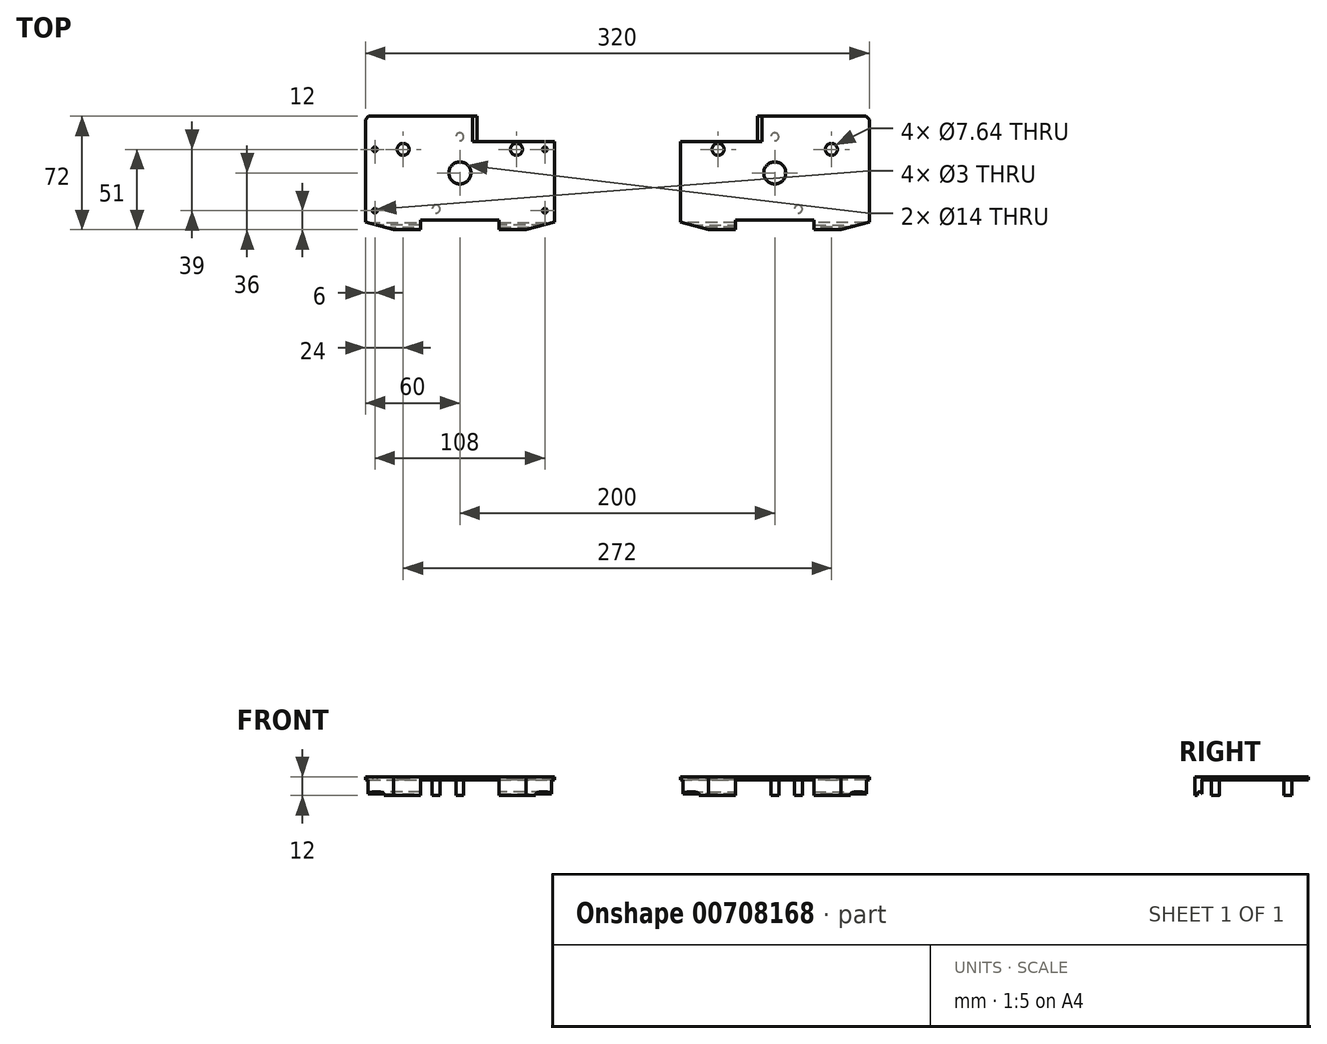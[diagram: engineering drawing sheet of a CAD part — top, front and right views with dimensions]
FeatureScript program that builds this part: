
annotation { "Feature Type Name" : "Feature", "Feature Type Description" : "" }
export const myFeature = defineFeature(function(context is Context, id is Id, definition is map)
    precondition{}
    {
        {
            var Q0;
            Q0=qCreatedBy(makeId("Top.planeOp"),FACE);
            var sketch = newSketch(context, id + "F0", { "sketchPlane" : qUnion([Q0])});
            skLineSegment(sketch, "E0.bottom", {"start": v(-60, 36) * mm, "end": v(60, 36) * mm});
            skLineSegment(sketch, "E0.top", {"start": v(-60, -36) * mm, "end": v(60, -36) * mm});
            skLineSegment(sketch, "E0.left", {"start": v(-60, 36) * mm, "end": v(-60, -36) * mm, "construction": true});
            skLineSegment(sketch, "E0.right", {"start": v(60, 36) * mm, "end": v(60, -36) * mm, "construction": true});
            skCircle(sketch, "E1", {"center": v(0, 0) * mm, "radius": 7 * mm});
            skLineSegment(sketch, "E2", {"start": v(-60, 0) * mm, "end": v(60, 0) * mm, "construction": true});
            skCircle(sketch, "E3", {"center": v(0, 23) * mm, "radius": 2.4 * mm, "construction": true});
            skCircle(sketch, "E4.0.MirrorC", {"center": v(0, -23) * mm, "radius": 2.4 * mm, "construction": true});
            skCircle(sketch, "E5.0.MirrorC", {"center": v(-15, 23) * mm, "radius": 2.5 * mm, "construction": true});
            skCircle(sketch, "E6.0.MirrorC", {"center": v(-15, -23) * mm, "radius": 2.5 * mm, "construction": true});
            skLineSegment(sketch, "E7.bottom", {"start": v(-22.32, 36) * mm, "end": v(10.24, 36) * mm, "construction": true});
            skLineSegment(sketch, "E7.top", {"start": v(-23.32, -36) * mm, "end": v(9.24, -36) * mm, "construction": true});
            skLineSegment(sketch, "E8.left", {"start": v(-60, 36) * mm, "end": v(-60, -36) * mm});
            skLineSegment(sketch, "E8.right", {"start": v(60, 36) * mm, "end": v(60, -36) * mm});
            skLineSegment(sketch, "E9.bottom", {"start": v(-60, 36) * mm, "end": v(-42, 36) * mm, "construction": true});
            skLineSegment(sketch, "E9.top", {"start": v(-60, -36) * mm, "end": v(-42, -36) * mm, "construction": true});
            skLineSegment(sketch, "E9.right", {"start": v(-42, 36) * mm, "end": v(-42, -36) * mm, "construction": true});
            skCircle(sketch, "E10", {"center": v(-36, 15) * mm, "radius": 3.82 * mm});
            skCircle(sketch, "E11.0.MirrorC", {"center": v(36, 15) * mm, "radius": 3.82 * mm});
            skLineSegment(sketch, "E12.bottom", {"start": v(10, -36) * mm, "end": v(-10, -36) * mm});
            skLineSegment(sketch, "E13", {"start": v(0, 23) * mm, "end": v(0, -23) * mm, "construction": true});
            skLineSegment(sketch, "E14", {"start": v(-36, 15) * mm, "end": v(0, 15) * mm, "construction": true});
            skLineSegment(sketch, "E15", {"start": v(0, 15) * mm, "end": v(36, 15) * mm, "construction": true});
            skCircle(sketch, "E16", {"center": v(-54, -24) * mm, "radius": 1.5 * mm, "construction": true});
            skCircle(sketch, "E17", {"center": v(-54, 15) * mm, "radius": 1.5 * mm, "construction": true});
            skLineSegment(sketch, "E18", {"start": v(-36, 15) * mm, "end": v(-56.54, 15) * mm, "construction": true});
            skLineSegment(sketch, "E19", {"start": v(-54, -24) * mm, "end": v(-54, 15) * mm, "construction": true});
            skCircle(sketch, "E20.0.MirrorC", {"center": v(54, 15) * mm, "radius": 1.5 * mm, "construction": true});
            skCircle(sketch, "E21.0.MirrorC", {"center": v(54, -24) * mm, "radius": 1.5 * mm, "construction": true});
            skSolve(sketch);
        }
        {
            var Q0;
            Q0=makeQuery(id+"F0.imprint","IMPRINT",FACE,{"disambiguationData":[TD([[makeQuery(id+"F0.imprint","IMPRINT",EDGE,{"derivedFrom":sQuery(id+"F0.wireOp",EDGE,"E1")}),-1.0]])]});
            extrude(context, id + "F1", {"entities" : qUnion([Q0]), "depth" : 12 * mm});
        }
        {
            var Q0;
            Q0=makeQuery(id+"F1.opExtrude","CAP_FACE",FACE,{"disambiguationData":[OSD([sQuery(id+"F0.wireOp",EDGE,"E1"),sQuery(id+"F0.wireOp",EDGE,"E0.bottom"),sQuery(id+"F0.wireOp",EDGE,"E0.top"),sQuery(id+"F0.wireOp",EDGE,"E8.left"),sQuery(id+"F0.wireOp",EDGE,"E8.right"),sQuery(id+"F0.wireOp",EDGE,"E10"),sQuery(id+"F0.wireOp",EDGE,"E11.0.MirrorC"),sQuery(id+"F0.wireOp",EDGE,"E12.bottom")])],"isStart":false});
            var sketch = newSketch(context, id + "F2", { "sketchPlane" : qUnion([Q0])});
            skLineSegment(sketch, "E22", {"start": v(60, 20) * mm, "end": v(60, 36) * mm});
            skLineSegment(sketch, "E23", {"start": v(60, 36) * mm, "end": v(-42, 36) * mm});
            skLineSegment(sketch, "E24", {"start": v(-60, -36) * mm, "end": v(60, -36) * mm});
            skLineSegment(sketch, "E25", {"start": v(-42, 20) * mm, "end": v(60, 20) * mm});
            skLineSegment(sketch, "E26", {"start": v(60, -36) * mm, "end": v(-60, -36) * mm});
            skLineSegment(sketch, "E27", {"start": v(-60, 36) * mm, "end": v(-42, 36) * mm, "construction": true});
            skLineSegment(sketch, "E28", {"start": v(60, 36) * mm, "end": v(60, 20) * mm});
            skLineSegment(sketch, "E29", {"start": v(-42, 36) * mm, "end": v(-42, 27) * mm, "construction": true});
            skLineSegment(sketch, "E30", {"start": v(-42, 27) * mm, "end": v(-46, 27) * mm, "construction": true});
            skLineSegment(sketch, "E31", {"start": v(-46, 27) * mm, "end": v(-46, 20) * mm, "construction": true});
            skLineSegment(sketch, "E32", {"start": v(-46, 20) * mm, "end": v(-42, 20) * mm, "construction": true});
            skSolve(sketch);
        }
        {
            var Q0;
            Q0=makeQuery(id+"F0.imprint","IMPRINT",FACE,{"disambiguationData":[TD([[makeQuery(id+"F0.imprint","IMPRINT",EDGE,{"derivedFrom":sQuery(id+"F0.wireOp",EDGE,"E1")}),-1.0]])]});
            var sketch = newSketch(context, id + "F3", { "sketchPlane" : qUnion([Q0])});
            skLineSegment(sketch, "E33.bottom", {"start": v(25, -36) * mm, "end": v(-25, -36) * mm});
            skLineSegment(sketch, "E33.top", {"start": v(25, -30) * mm, "end": v(-25, -30) * mm});
            skLineSegment(sketch, "E33.left", {"start": v(25, -36) * mm, "end": v(25, -30) * mm});
            skLineSegment(sketch, "E33.right", {"start": v(-25, -36) * mm, "end": v(-25, -30) * mm});
            skLineSegment(sketch, "E34", {"start": v(-25, -33) * mm, "end": v(0, -33) * mm, "construction": true});
            skLineSegment(sketch, "E35", {"start": v(0, -33) * mm, "end": v(25, -33) * mm, "construction": true});
            skLineSegment(sketch, "E36", {"start": v(0, -22.48) * mm, "end": v(0, -36) * mm, "construction": true});
            skSolve(sketch);
        }
        {
            var Q0;
            Q0=makeQuery(id+"F3.imprint","IMPRINT",FACE,{"disambiguationData":[TD([[makeQuery(id+"F3.imprint","IMPRINT",EDGE,{"derivedFrom":sQuery(id+"F3.wireOp",EDGE,"E33.top")}),1.0]])]});
            var Q1;
            Q1=makeQuery(id+"F1.opExtrude","CAP_FACE",FACE,{"disambiguationData":[OSD([sQuery(id+"F0.wireOp",EDGE,"E1"),sQuery(id+"F0.wireOp",EDGE,"E0.bottom"),sQuery(id+"F0.wireOp",EDGE,"E0.top"),sQuery(id+"F0.wireOp",EDGE,"E8.left"),sQuery(id+"F0.wireOp",EDGE,"E8.right"),sQuery(id+"F0.wireOp",EDGE,"E10"),sQuery(id+"F0.wireOp",EDGE,"E11.0.MirrorC"),sQuery(id+"F0.wireOp",EDGE,"E12.bottom")])],"isStart":false});
            extrude(context, id + "F4", {"entities" : qUnion([Q0]), "operationType" : NewBodyOperationType.REMOVE, "endBound" : BoundingType.UP_TO_SURFACE, "endBoundEntityFace" : qUnion([Q1]), "depth" : 25 * mm});
        }
        {
            var Q0;
            Q0=makeQuery(id+"F0.imprint","IMPRINT",FACE,{"disambiguationData":[TD([[makeQuery(id+"F0.imprint","IMPRINT",EDGE,{"derivedFrom":sQuery(id+"F0.wireOp",EDGE,"E1")}),-1.0]])]});
            var sketch = newSketch(context, id + "F5", { "sketchPlane" : qUnion([Q0])});
            skLineSegment(sketch, "E37.bottom", {"start": v(-60, -31.62) * mm, "end": v(60, -31.63) * mm});
            skLineSegment(sketch, "E37.top", {"start": v(-60, -34.37) * mm, "end": v(60, -34.38) * mm});
            skLineSegment(sketch, "E37.left", {"start": v(-60, -31.62) * mm, "end": v(-60, -34.37) * mm});
            skLineSegment(sketch, "E37.right", {"start": v(60, -31.63) * mm, "end": v(60, -34.38) * mm});
            skLineSegment(sketch, "E38", {"start": v(8.47, -31.63) * mm, "end": v(8.47, -30) * mm, "construction": true});
            skLineSegment(sketch, "E39", {"start": v(8.43, -34.38) * mm, "end": v(8.43, -36) * mm, "construction": true});
            skSolve(sketch);
        }
        {
            var Q0;
            Q0=makeQuery(id+"F5.imprint","IMPRINT",FACE,{"disambiguationData":[TD([[makeQuery(id+"F5.imprint","IMPRINT",EDGE,{"derivedFrom":sQuery(id+"F5.wireOp",EDGE,"E37.bottom")}),-1.0]])]});
            extrude(context, id + "F6", {"entities" : qUnion([Q0]), "operationType" : NewBodyOperationType.REMOVE, "depth" : 2.5 * mm});
        }
        {
            var Q0;
            Q0=makeQuery(id+"F6.boolean.opBoolean","COPY",EDGE,{"disambiguationData":[OD(1.0)],"derivedFrom":makeQuery(id+"F6.opExtrude","CAP_EDGE",EDGE,{"disambiguationData":[OSD([sQuery(id+"F5.wireOp",EDGE,"E37.bottom")])],"isStart":false})});
            var Q1;
            Q1=makeQuery(id+"F6.boolean.opBoolean","COPY",EDGE,{"disambiguationData":[OD(1.0)],"derivedFrom":makeQuery(id+"F6.opExtrude","CAP_EDGE",EDGE,{"disambiguationData":[OSD([sQuery(id+"F5.wireOp",EDGE,"E37.top")])],"isStart":false})});
            var Q2;
            Q2=makeQuery(id+"F6.boolean.opBoolean","COPY",EDGE,{"disambiguationData":[OD(0.0)],"derivedFrom":makeQuery(id+"F6.opExtrude","CAP_EDGE",EDGE,{"disambiguationData":[OSD([sQuery(id+"F5.wireOp",EDGE,"E37.top")])],"isStart":false})});
            var Q3;
            Q3=makeQuery(id+"F6.boolean.opBoolean","COPY",EDGE,{"disambiguationData":[OD(0.0)],"derivedFrom":makeQuery(id+"F6.opExtrude","CAP_EDGE",EDGE,{"disambiguationData":[OSD([sQuery(id+"F5.wireOp",EDGE,"E37.bottom")])],"isStart":false})});
            fillet(context, id + "F7", {"entities" : qUnion([Q0, Q1, Q2, Q3]), "radius" : 1.5 * mm, "tangentPropagation" : true, "allowEdgeOverflow" : false});
        }
        {
            var Q0;
            Q0=makeQuery(id+"F1.opExtrude","SWEPT_FACE",FACE,{"disambiguationData":[OSD([sQuery(id+"F0.wireOp",EDGE,"E0.bottom")])]});
            var sketch = newSketch(context, id + "F8", { "sketchPlane" : qUnion([Q0])});
            skLineSegment(sketch, "E40", {"start": v(-60, 6) * mm, "end": v(-38.5, 6) * mm, "construction": true});
            skLineSegment(sketch, "E41", {"start": v(0, 0) * mm, "end": v(0, 12) * mm, "construction": true});
            skLineSegment(sketch, "E42", {"start": v(-8, 0) * mm, "end": v(-8, 12) * mm, "construction": true});
            skLineSegment(sketch, "E43", {"start": v(-8, 12) * mm, "end": v(-60, 12) * mm});
            skLineSegment(sketch, "E44", {"start": v(-60, 2) * mm, "end": v(-60, 12) * mm});
            skLineSegment(sketch, "E45", {"start": v(-8, 2) * mm, "end": v(-23.25, 2) * mm, "construction": true});
            skLineSegment(sketch, "E46", {"start": v(-23.25, 2) * mm, "end": v(-38.5, 2) * mm, "construction": true});
            skLineSegment(sketch, "E47", {"start": v(-38.5, 6) * mm, "end": v(-38.5, 0) * mm, "construction": true});
            skLineSegment(sketch, "E48", {"start": v(-60, 2) * mm, "end": v(-23.25, 2) * mm});
            skLineSegment(sketch, "E49", {"start": v(-23.25, 2) * mm, "end": v(-8, 12) * mm});
            skSolve(sketch);
        }
        {
            var Q0;
            Q0=makeQuery(id+"F8.imprint","IMPRINT",FACE,{"disambiguationData":[TD([[makeQuery(id+"F8.imprint","IMPRINT",EDGE,{"derivedFrom":sQuery(id+"F8.wireOp",EDGE,"E43")}),1.0]])]});
            extrude(context, id + "F9", {"entities" : qUnion([Q0]), "operationType" : NewBodyOperationType.REMOVE, "oppositeDirection" : true, "depth" : 16 * mm});
        }
        {
            var Q0;
            Q0=makeQuery(id+"F9.boolean.opBoolean","COPY",EDGE,{"derivedFrom":makeQuery(id+"F9.opExtrude","SWEPT_EDGE",EDGE,{"disambiguationData":[OSD([sQuery(id+"F8.wireOp",EDGE,"dc820323-19ea-4039-b468-714fe8b4bf2b"),sQuery(id+"F8.wireOp",EDGE,"f9c62189-2ec5-4655-88e0-a14efa9e9823")])]})});
            var Q1;
            Q1=makeQuery(id+"F9.boolean.opBoolean","COPY",EDGE,{"derivedFrom":makeQuery(id+"F9.opExtrude","SWEPT_EDGE",EDGE,{"disambiguationData":[OSD([sQuery(id+"F2.wireOp",EDGE,"E23"),sQuery(id+"F8.wireOp",EDGE,"f9c62189-2ec5-4655-88e0-a14efa9e9823"),sQuery(id+"F8.wireOp",EDGE,"E43")])]})});
            var Q2;
            Q2=makeQuery(id+"F9.boolean.opBoolean","COPY",EDGE,{"derivedFrom":makeQuery(id+"F9.opExtrude","SWEPT_EDGE",EDGE,{"disambiguationData":[OSD([sQuery(id+"F8.wireOp",EDGE,"E48"),sQuery(id+"F8.wireOp",EDGE,"E49")])]})});
            var Q3;
            Q3=makeQuery(id+"F9.boolean.opBoolean","COPY",EDGE,{"derivedFrom":makeQuery(id+"F9.opExtrude","SWEPT_EDGE",EDGE,{"disambiguationData":[OSD([sQuery(id+"F0.wireOp",EDGE,"E0.bottom"),sQuery(id+"F8.wireOp",EDGE,"E43"),sQuery(id+"F8.wireOp",EDGE,"E49")])]})});
            fillet(context, id + "F10", {"entities" : qUnion([Q0, Q1, Q2, Q3]), "radius" : 5 * mm, "tangentPropagation" : true, "allowEdgeOverflow" : false});
        }
        {
            var Q0;
            {var subQ0=sQuery(id+"F0.wireOp",EDGE,"E1");var subQ1=sQuery(id+"F0.wireOp",EDGE,"E0.bottom");var subQ2=sQuery(id+"F0.wireOp",EDGE,"E8.left");var subQ3=sQuery(id+"F0.wireOp",EDGE,"E8.right");var subQ4=sQuery(id+"F0.wireOp",EDGE,"E10");var subQ5=sQuery(id+"F0.wireOp",EDGE,"E11.0.MirrorC");Q0=makeQuery(id+"F6.boolean.opBoolean","SPLIT",FACE,{"disambiguationData":[TD([makeQuery(id+"F1.opExtrude","SWEPT_FACE",FACE,{"disambiguationData":[OSD([subQ0])]}),makeQuery(id+"F1.opExtrude","SWEPT_FACE",FACE,{"disambiguationData":[OSD([subQ1])]}),makeQuery(id+"F1.opExtrude","SWEPT_FACE",FACE,{"disambiguationData":[OSD([subQ2])]}),makeQuery(id+"F1.opExtrude","SWEPT_FACE",FACE,{"disambiguationData":[OSD([subQ3])]}),makeQuery(id+"F1.opExtrude","SWEPT_FACE",FACE,{"disambiguationData":[OSD([subQ4])]}),makeQuery(id+"F1.opExtrude","SWEPT_FACE",FACE,{"disambiguationData":[OSD([subQ5])]}),makeQuery(id+"F4.boolean.opBoolean","COPY",FACE,{"derivedFrom":makeQuery(id+"F4.opExtrude","SWEPT_FACE",FACE,{"disambiguationData":[OSD([sQuery(id+"F3.wireOp",EDGE,"E33.top")])]})}),makeQuery(id+"F4.boolean.opBoolean","COPY",FACE,{"derivedFrom":makeQuery(id+"F4.opExtrude","SWEPT_FACE",FACE,{"disambiguationData":[OSD([sQuery(id+"F3.wireOp",EDGE,"E33.left")])]})}),makeQuery(id+"F4.boolean.opBoolean","COPY",FACE,{"derivedFrom":makeQuery(id+"F4.opExtrude","SWEPT_FACE",FACE,{"disambiguationData":[OSD([sQuery(id+"F3.wireOp",EDGE,"E33.right")])]})}),makeQuery(id+"F6.opExtrude","SWEPT_FACE",FACE,{"disambiguationData":[OSD([sQuery(id+"F5.wireOp",EDGE,"E37.bottom")])]})])],"derivedFrom":makeQuery(id+"F1.opExtrude","CAP_FACE",FACE,{"disambiguationData":[OSD([subQ0,subQ1,sQuery(id+"F0.wireOp",EDGE,"E0.top"),subQ2,subQ3,subQ4,subQ5,sQuery(id+"F0.wireOp",EDGE,"E12.bottom")])],"isStart":true})});}
            var sketch = newSketch(context, id + "F11", { "sketchPlane" : qUnion([Q0])});
            skCircle(sketch, "E50", {"center": v(-15.05, -22.91) * mm, "radius": 2.5 * mm});
            skCircle(sketch, "E51.0.MirrorC", {"center": v(-0.05, -23) * mm, "radius": 2.5 * mm});
            skCircle(sketch, "E52.0.MirrorC", {"center": v(-15.05, 22.91) * mm, "radius": 2.5 * mm});
            skCircle(sketch, "E53.0.MirrorC", {"center": v(-0.05, 23) * mm, "radius": 2.5 * mm});
            skSolve(sketch);
        }
        {
            var Q0;
            {Q0=qUnion([makeQuery(id+"F11.imprint","IMPRINT",FACE,{"disambiguationData":[TD([[makeQuery(id+"F11.imprint","IMPRINT",EDGE,{"derivedFrom":sQuery(id+"F11.wireOp",EDGE,"E50")}),1.0]])]}),makeQuery(id+"F11.imprint","IMPRINT",FACE,{"disambiguationData":[TD([[makeQuery(id+"F11.imprint","IMPRINT",EDGE,{"derivedFrom":sQuery(id+"F11.wireOp",EDGE,"E51.0.MirrorC")}),-1.0]])]}),makeQuery(id+"F11.imprint","IMPRINT",FACE,{"disambiguationData":[TD([[makeQuery(id+"F11.imprint","IMPRINT",EDGE,{"derivedFrom":sQuery(id+"F11.wireOp",EDGE,"E52.0.MirrorC")}),-1.0]])]}),makeQuery(id+"F11.imprint","IMPRINT",FACE,{"disambiguationData":[TD([[makeQuery(id+"F11.imprint","IMPRINT",EDGE,{"derivedFrom":sQuery(id+"F11.wireOp",EDGE,"E53.0.MirrorC")}),1.0]])]})]);}
            extrude(context, id + "F12", {"entities" : qUnion([Q0]), "operationType" : NewBodyOperationType.REMOVE, "oppositeDirection" : true, "depth" : 10 * mm});
        }
        {
            var Q0;
            Q0=makeQuery(id+"F0.imprint","IMPRINT",FACE,{"disambiguationData":[TD([[makeQuery(id+"F0.imprint","IMPRINT",EDGE,{"derivedFrom":sQuery(id+"F0.wireOp",EDGE,"E1")}),-1.0]])]});
            var sketch = newSketch(context, id + "F13", { "sketchPlane" : qUnion([Q0])});
            skLineSegment(sketch, "E54", {"start": v(-60, -31.12) * mm, "end": v(-42, -36) * mm});
            skLineSegment(sketch, "E55", {"start": v(-42, -36) * mm, "end": v(-60, -36) * mm});
            skLineSegment(sketch, "E56", {"start": v(-60, -36) * mm, "end": v(-60, -31.12) * mm});
            skPoint(sketch, "E57", {"position": v(-60, -31.62) * mm});
            skLineSegment(sketch, "E58.MirrorCS", {"start": v(60, -31.12) * mm, "end": v(42, -36) * mm});
            skLineSegment(sketch, "E59.MirrorCS", {"start": v(60, -36) * mm, "end": v(60, -31.12) * mm});
            skLineSegment(sketch, "E60.MirrorCS", {"start": v(42, -36) * mm, "end": v(60, -36) * mm});
            skSolve(sketch);
        }
        {
            var Q0;
            Q0=qSketchRegion(id+"F13",true);
            var Q1;
            Q1=makeQuery(id+"F1.opExtrude","CAP_FACE",FACE,{"disambiguationData":[OSD([sQuery(id+"F0.wireOp",EDGE,"E1"),sQuery(id+"F0.wireOp",EDGE,"E0.bottom"),sQuery(id+"F0.wireOp",EDGE,"E0.top"),sQuery(id+"F0.wireOp",EDGE,"E8.left"),sQuery(id+"F0.wireOp",EDGE,"E8.right"),sQuery(id+"F0.wireOp",EDGE,"E10"),sQuery(id+"F0.wireOp",EDGE,"E11.0.MirrorC"),sQuery(id+"F0.wireOp",EDGE,"E12.bottom")])],"isStart":false});
            extrude(context, id + "F14", {"entities" : qUnion([Q0]), "operationType" : NewBodyOperationType.REMOVE, "endBound" : BoundingType.UP_TO_SURFACE, "endBoundEntityFace" : qUnion([Q1]), "depth" : 25 * mm});
        }
        {
            var Q0;
            Q0=makeQuery(id+"F1.opExtrude","SWEPT_EDGE",EDGE,{"disambiguationData":[OSD([sQuery(id+"F0.wireOp",EDGE,"E0.bottom"),sQuery(id+"F0.wireOp",EDGE,"E8.left")])]});
            chamfer(context, id + "F15", {"entities" : qUnion([Q0]), "width" : 2 * mm, "tangentPropagation" : true});
        }
        {
            var Q0;
            Q0=qCreatedBy(makeId("Right.planeOp"),FACE);
            cPlane(context, id + "F16", {"entities" : qUnion([Q0]), "cplaneType" : CPlaneType.OFFSET, "offset" : 100 * mm, "width" : 150 * mm, "height" : 150 * mm});
        }
        {
            var Q0;
            Q0=makeQuery(id+"F1.opExtrude","SWEPT_BODY",BODY,{"disambiguationData":[OSD([sQuery(id+"F0.wireOp",EDGE,"E1"),sQuery(id+"F0.wireOp",EDGE,"E0.bottom"),sQuery(id+"F0.wireOp",EDGE,"E0.top"),sQuery(id+"F0.wireOp",EDGE,"E8.left"),sQuery(id+"F0.wireOp",EDGE,"E8.right"),sQuery(id+"F0.wireOp",EDGE,"E10"),sQuery(id+"F0.wireOp",EDGE,"E11.0.MirrorC"),sQuery(id+"F0.wireOp",EDGE,"E12.bottom")])]});
            var Q1;
            Q1=qCreatedBy(id+"F16.planeOp",FACE);
            mirror(context, id + "F17", {"entities" : qUnion([Q0]), "mirrorPlane" : qUnion([Q1])});
        }
        {
            var Q0;
            Q0=qCreatedBy(makeId("Top.planeOp"),FACE);
            var sketch = newSketch(context, id + "F18", { "sketchPlane" : qUnion([Q0])});
            skCircle(sketch, "E61", {"center": v(-54, -24) * mm, "radius": 1.5 * mm});
            skCircle(sketch, "E62", {"center": v(-54, 15) * mm, "radius": 1.5 * mm});
            skCircle(sketch, "E63", {"center": v(54, 15) * mm, "radius": 1.5 * mm});
            skCircle(sketch, "E64", {"center": v(54, -24) * mm, "radius": 1.5 * mm});
            skSolve(sketch);
        }
        {
            var Q0;
            {Q0=qUnion([makeQuery(id+"F18.imprint","IMPRINT",FACE,{"disambiguationData":[TD([[makeQuery(id+"F18.imprint","IMPRINT",EDGE,{"derivedFrom":sQuery(id+"F18.wireOp",EDGE,"E61")}),1.0]])]}),makeQuery(id+"F18.imprint","IMPRINT",FACE,{"disambiguationData":[TD([[makeQuery(id+"F18.imprint","IMPRINT",EDGE,{"derivedFrom":sQuery(id+"F18.wireOp",EDGE,"E62")}),1.0]])]}),makeQuery(id+"F18.imprint","IMPRINT",FACE,{"disambiguationData":[TD([[makeQuery(id+"F18.imprint","IMPRINT",EDGE,{"derivedFrom":sQuery(id+"F18.wireOp",EDGE,"E63")}),1.0]])]}),makeQuery(id+"F18.imprint","IMPRINT",FACE,{"disambiguationData":[TD([[makeQuery(id+"F18.imprint","IMPRINT",EDGE,{"derivedFrom":sQuery(id+"F18.wireOp",EDGE,"E64")}),1.0]])]})]);}
            var Q1;
            Q1=makeQuery(id+"F1.opExtrude","CAP_FACE",FACE,{"disambiguationData":[OSD([sQuery(id+"F0.wireOp",EDGE,"E1"),sQuery(id+"F0.wireOp",EDGE,"E0.bottom"),sQuery(id+"F0.wireOp",EDGE,"E0.top"),sQuery(id+"F0.wireOp",EDGE,"E8.left"),sQuery(id+"F0.wireOp",EDGE,"E8.right"),sQuery(id+"F0.wireOp",EDGE,"E10"),sQuery(id+"F0.wireOp",EDGE,"E11.0.MirrorC"),sQuery(id+"F0.wireOp",EDGE,"E12.bottom")])],"isStart":false});
            extrude(context, id + "F19", {"entities" : qUnion([Q0]), "operationType" : NewBodyOperationType.REMOVE, "endBound" : BoundingType.UP_TO_SURFACE, "endBoundEntityFace" : qUnion([Q1]), "depth" : 25 * mm});
        }
        {
            var Q0;
            Q0=qCreatedBy(makeId("Top.planeOp"),FACE);
            var sketch = newSketch(context, id + "F20", { "sketchPlane" : qUnion([Q0])});
            skCircle(sketch, "E65", {"center": v(-54, -24) * mm, "radius": 3 * mm});
            skCircle(sketch, "E66", {"center": v(-54, 15) * mm, "radius": 3 * mm});
            skCircle(sketch, "E67", {"center": v(54, 15) * mm, "radius": 3 * mm});
            skCircle(sketch, "E68", {"center": v(54, -24) * mm, "radius": 3 * mm});
            skSolve(sketch);
        }
        {
            var Q0;
            {Q0=qUnion([makeQuery(id+"F20.imprint","IMPRINT",FACE,{"disambiguationData":[TD([[makeQuery(id+"F20.imprint","IMPRINT",EDGE,{"derivedFrom":sQuery(id+"F20.wireOp",EDGE,"E65")}),1.0]])]}),makeQuery(id+"F20.imprint","IMPRINT",FACE,{"disambiguationData":[TD([[makeQuery(id+"F20.imprint","IMPRINT",EDGE,{"derivedFrom":sQuery(id+"F20.wireOp",EDGE,"E66")}),1.0]])]}),makeQuery(id+"F20.imprint","IMPRINT",FACE,{"disambiguationData":[TD([[makeQuery(id+"F20.imprint","IMPRINT",EDGE,{"derivedFrom":sQuery(id+"F20.wireOp",EDGE,"E67")}),1.0]])]}),makeQuery(id+"F20.imprint","IMPRINT",FACE,{"disambiguationData":[TD([[makeQuery(id+"F20.imprint","IMPRINT",EDGE,{"derivedFrom":sQuery(id+"F20.wireOp",EDGE,"E68")}),1.0]])]})]);}
            extrude(context, id + "F21", {"entities" : qUnion([Q0]), "operationType" : NewBodyOperationType.REMOVE, "depth" : 3 * mm});
        }
    });
